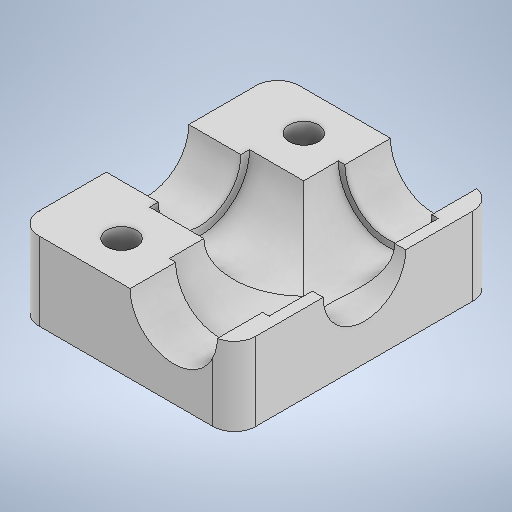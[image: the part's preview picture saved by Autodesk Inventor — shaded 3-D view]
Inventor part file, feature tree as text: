
AUTODESK INVENTOR PART (.ipt)
format: ipt  version: 2025 (Build 290162000, 162)  size: 314,368 bytes
history: native  units: mm
features: sketch x7, extrude x6, plane x1, hole x1, fillet x1
ambient origin geometry x8: Origin, YZ Plane, XZ Plane, XY Plane, X Axis, Y Axis, Z Axis, Center Point
bodies: Solid1 (feature_tree)
feature tree (16):
  extrude  "Extrusion1"  Depth=60.0mm
  extrude  "Extrusion2"  Depth=18.0mm
  extrude  "Extrusion3"  Depth=20.0mm
  extrude  "Extrusion4"  TaperAngle=0.0deg  [1 undecoded]
  plane  "Work Plane2"
  extrude  "Extrusion5"  Depth=39.0mm TaperAngle=0.0deg
  hole  "Hole2"  [1 undecoded]
  fillet  "Fillet1"  Radius=9.0mm
  extrude  "Extrusion6"  Depth=6.35mm
  sketch  "Sketch1"  dims[d0=50.0mm d1=60.0mm]
  sketch  "Sketch2"  dims[d2=18.0mm d3=0.0mm d4=19.0mm]
  sketch  "Sketch3"  dims[d5=0.0mm d6=0.0mm d7=20.0mm]
  sketch  "Sketch4"  dims[d8=14.0mm d9=0.0mm d10=0.0mm]
  sketch  "Sketch5"  dims[d11=23.0mm d12=39.0mm d13=0.0mm]
  sketch  "Sketch7"  dims[d14=23.0mm d15=24.0mm d16=0.0mm d28=9.0mm]
  sketch  "Sketch8"  dims[d29=9.0mm d30=15.0mm d31=6.756mm d32=6.0mm d33=11.113mm d34=6.35mm d35=90.0deg d36=8.0mm d37=20.594885mm d38=5.0mm d39=11.43mm d40=11.43mm d41=11.43mm d42=11.43mm d43=6.35mm d44=0.0mm]
note: 2 required parameter values undecoded (feature->parameter linkage not recoverable at this tier; creation-order binding heuristic only, values carry confidence <= 0.55)
